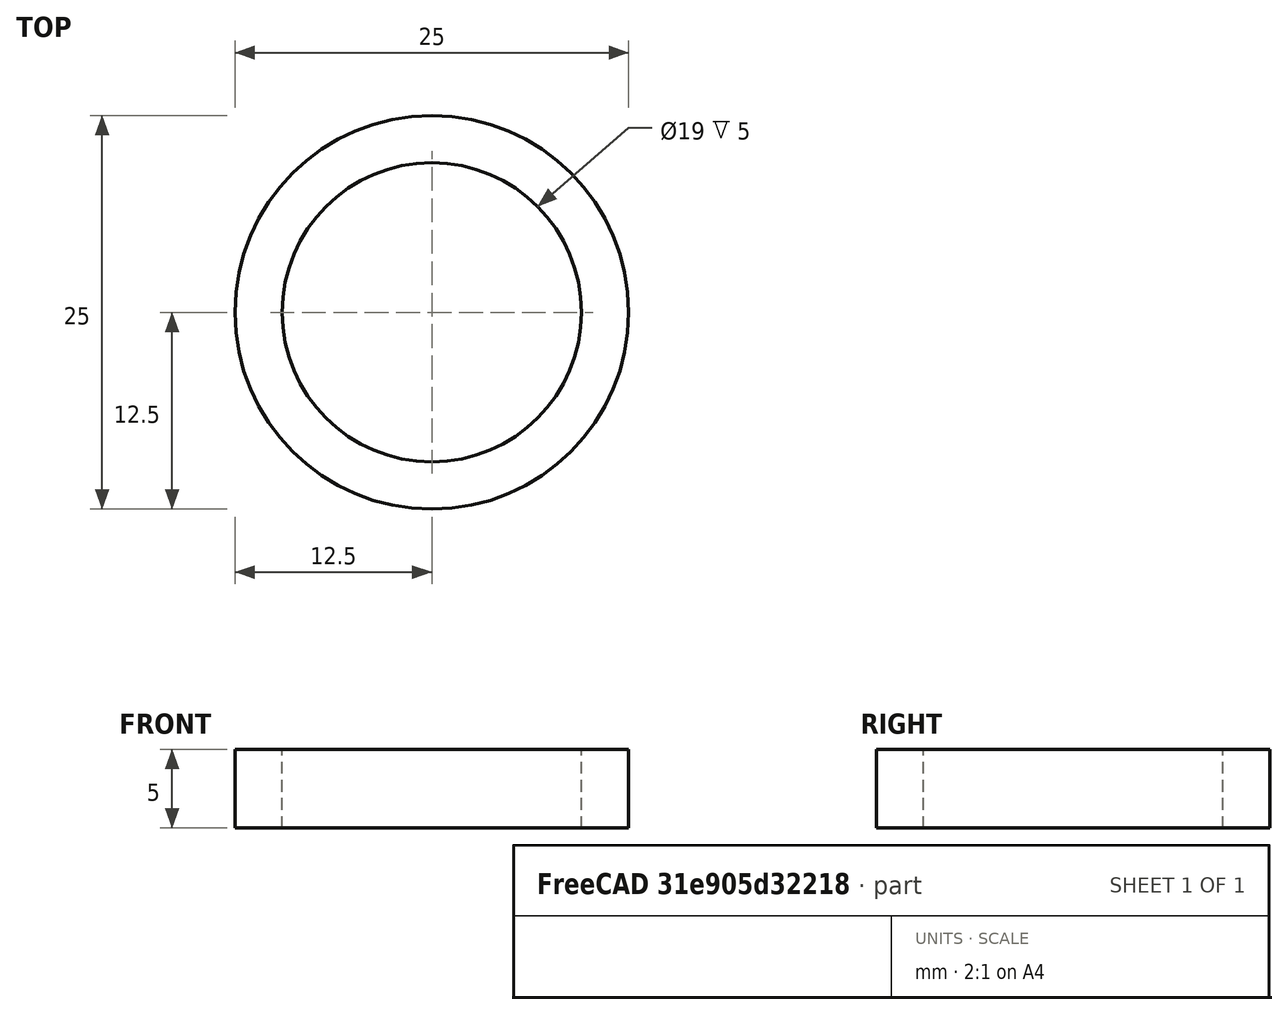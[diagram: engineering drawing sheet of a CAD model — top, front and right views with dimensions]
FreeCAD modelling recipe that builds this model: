
FCSTD DOCUMENT  (FreeCAD 0.16R6707 (Git))
Label: 01-anillo-osito
License: All rights reserved
LicenseURL: http://en.wikipedia.org/wiki/All_rights_reserved
objects: Part::Cylinder×2, Part::Cut×1, Spreadsheet::Sheet×1
note: 3 computed .brp shape members not serialized (recipe doc carries the construction recipe); baked Part::Feature solids carry a one-line shape summary decoded from their .brp

FEATURE [Part::Cylinder] Cylinder  label="Cilindro-exterior"
  Angle = 360
  Height = 5
  Radius = 12.5
  expr: Height = param.alt
  expr: Radius = param.di / 2 + param.gr
FEATURE [Part::Cylinder] Cylinder001  label="Cilindro-interior"
  Angle = 360
  Height = 15
  Placement = pos=(0,0,-4) rot=(0,0,1;0rad)
  Radius = 9.5
  expr: Height = param.alt + 10
  expr: Radius = param.di / 2
FEATURE [Part::Cut] Cut  label="cuerpo-anillo"
  Base = -> Cylinder
  Tool = -> Cylinder001
FEATURE [Spreadsheet::Sheet] Spreadsheet  label="param"
  cells = C3=Diametro interior; D3(di)=19; E3=19; C4=Grosor; D4(gr)=3; E4=3; C5=Altura; D5(alt)=5; E5=5
